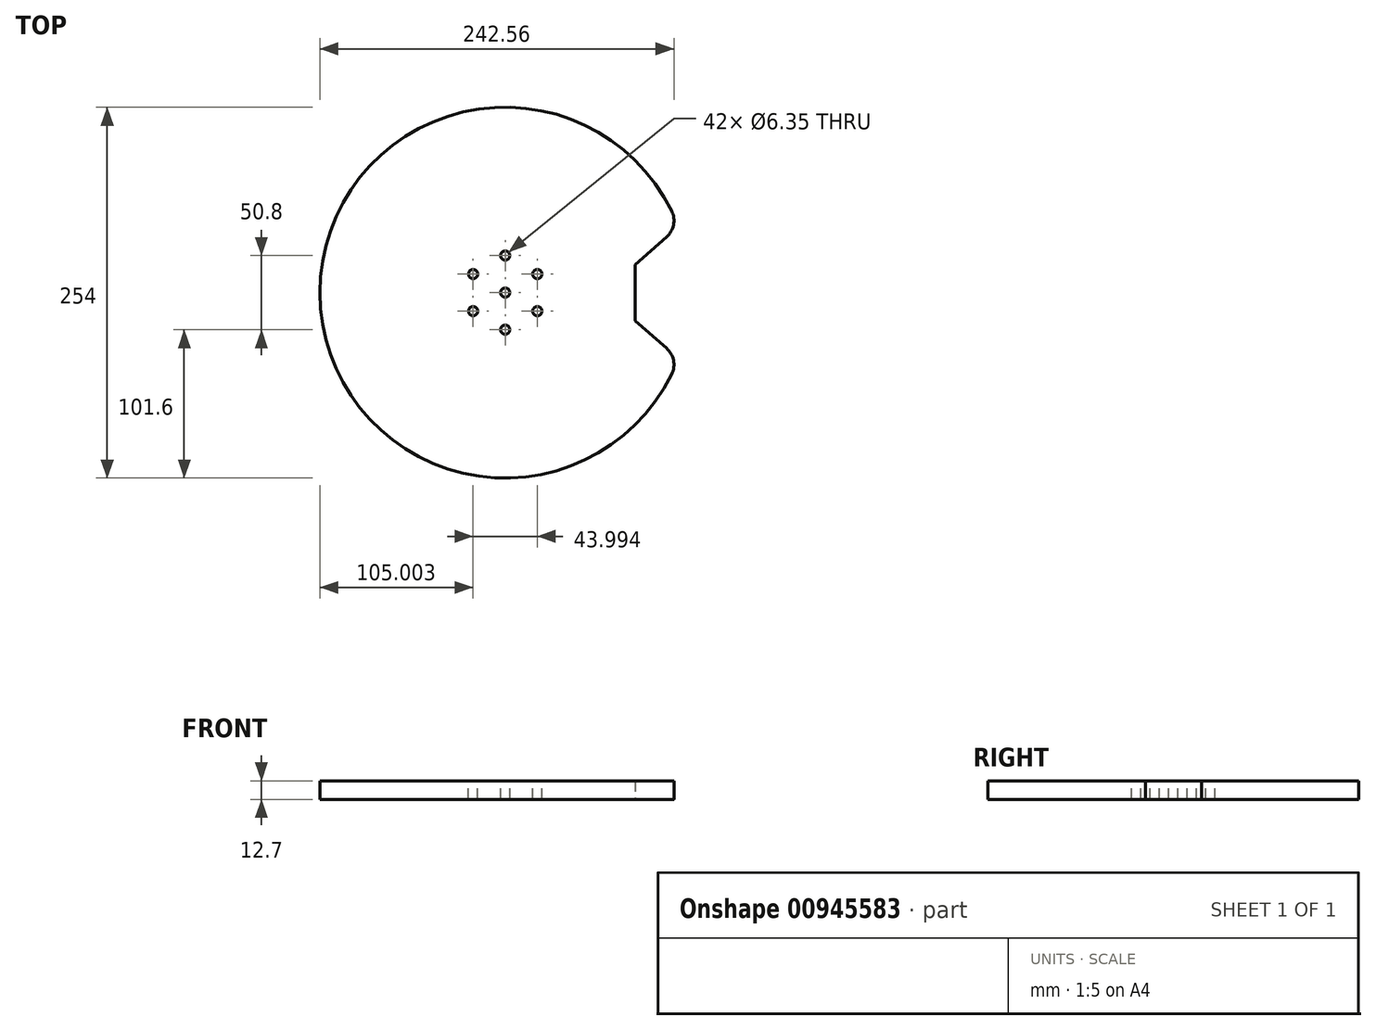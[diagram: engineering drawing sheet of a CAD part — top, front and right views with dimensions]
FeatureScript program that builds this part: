
annotation { "Feature Type Name" : "Feature", "Feature Type Description" : "" }
export const myFeature = defineFeature(function(context is Context, id is Id, definition is map)
    precondition{}
    {
        {
            var Q0;
            Q0=qCreatedBy(makeId("Top.planeOp"),FACE);
            var sketch = newSketch(context, id + "F0", { "sketchPlane" : qUnion([Q0])});
            skCircle(sketch, "E0", {"center": v(0, 0) * mm, "radius": 127 * mm});
            skLineSegment(sketch, "E1", {"start": v(88.9, 90.7) * mm, "end": v(88.9, -90.7) * mm});
            skLineSegment(sketch, "E2", {"start": v(88.9, 0) * mm, "end": v(127, 0) * mm});
            skSolve(sketch);
        }
        {
            var Q0;
            Q0=qCreatedBy(makeId("Top.planeOp"),FACE);
            var sketch = newSketch(context, id + "F1", { "sketchPlane" : qUnion([Q0])});
            skLineSegment(sketch, "E3", {"start": v(88.9, 19.18) * mm, "end": v(88.9, -19.18) * mm});
            skLineSegment(sketch, "E4", {"start": v(127, 52.5) * mm, "end": v(127, -52.5) * mm});
            skLineSegment(sketch, "E5", {"start": v(88.9, 19.18) * mm, "end": v(127, 52.5) * mm});
            skLineSegment(sketch, "E6", {"start": v(88.9, -19.18) * mm, "end": v(127, -52.5) * mm});
            skSolve(sketch);
        }
        {
            var Q0;
            {var subQ0=sQuery(id+"F0.wireOp",EDGE,"E1");var subQ1=sQuery(id+"F0.wireOp",EDGE,"E0");var subQ2=makeQuery(id+"F0.imprint","INTERSECT",VERTEX,{"disambiguationData":[OD(0.0)],"derivedFrom":[subQ1,subQ0]});Q0=makeQuery(id+"F0.imprint","IMPRINT",FACE,{"disambiguationData":[TD([[makeQuery(id+"F0.imprint","IMPRINT",EDGE,{"disambiguationData":[TD([[subQ2,-1.0]])],"derivedFrom":subQ1}),1.0]])]});}
            var Q1;
            {var subQ3=sQuery(id+"F0.wireOp",EDGE,"E2");Q1=makeQuery(id+"F0.imprint","IMPRINT",FACE,{"disambiguationData":[TD([[makeQuery(id+"F0.imprint","IMPRINT",EDGE,{"derivedFrom":subQ3}),1.0]])]});}
            var Q2;
            {var subQ3=sQuery(id+"F0.wireOp",EDGE,"E2");Q2=makeQuery(id+"F0.imprint","IMPRINT",FACE,{"disambiguationData":[TD([[makeQuery(id+"F0.imprint","IMPRINT",EDGE,{"derivedFrom":subQ3}),-1.0]])]});}
            extrude(context, id + "F2", {"entities" : qUnion([Q0, Q1, Q2]), "depth" : 12.7 * mm, "offsetDistance" : 25 * mm});
        }
        {
            var Q0;
            Q0=qSketchRegion(id+"F1",true);
            var Q1;
            Q1=makeQuery(id+"F2.opExtrude","CAP_FACE",FACE,{"disambiguationData":[OSD([sQuery(id+"F0.wireOp",EDGE,"E0")])],"isStart":false});
            extrude(context, id + "F3", {"entities" : qUnion([Q0]), "operationType" : NewBodyOperationType.REMOVE, "endBound" : BoundingType.UP_TO_SURFACE, "depth" : 25 * mm, "endBoundEntityFace" : qUnion([Q1]), "offsetDistance" : 25 * mm});
        }
        {
            var Q0;
            Q0=makeQuery(id+"F3.boolean.opBoolean","INTERSECT",EDGE,{"derivedFrom":[makeQuery(id+"F2.opExtrude","SWEPT_FACE",FACE,{"disambiguationData":[OSD([sQuery(id+"F0.wireOp",EDGE,"E0")])]}),makeQuery(id+"F3.opExtrude","SWEPT_FACE",FACE,{"disambiguationData":[OSD([sQuery(id+"F1.wireOp",EDGE,"E6")])]})]});
            var Q1;
            Q1=makeQuery(id+"F3.boolean.opBoolean","INTERSECT",EDGE,{"derivedFrom":[makeQuery(id+"F2.opExtrude","SWEPT_FACE",FACE,{"disambiguationData":[OSD([sQuery(id+"F0.wireOp",EDGE,"E0")])]}),makeQuery(id+"F3.opExtrude","SWEPT_FACE",FACE,{"disambiguationData":[OSD([sQuery(id+"F1.wireOp",EDGE,"E5")])]})]});
            fillet(context, id + "F4", {"entities" : qUnion([Q0, Q1]), "radius" : 15 * mm, "tangentPropagation" : true, "allowEdgeOverflow" : false});
        }
        {
            var Q0;
            Q0=makeQuery(id+"F2.opExtrude","CAP_FACE",FACE,{"disambiguationData":[OSD([sQuery(id+"F0.wireOp",EDGE,"E0")])],"isStart":false});
            var sketch = newSketch(context, id + "F5", { "sketchPlane" : qUnion([Q0])});
            skCircle(sketch, "E7", {"center": v(0, 0) * mm, "radius": 3.17 * mm});
            skCircle(sketch, "E8.cCircle", {"center": v(0, 0) * mm, "radius": 25.4 * mm, "construction": true});
            skLineSegment(sketch, "E8.0", {"start": v(0, -25.4) * mm, "end": v(-22, -12.7) * mm, "construction": true});
            skLineSegment(sketch, "E8.1", {"start": v(-22, -12.7) * mm, "end": v(-22, 12.7) * mm, "construction": true});
            skLineSegment(sketch, "E8.2", {"start": v(-22, 12.7) * mm, "end": v(0, 25.4) * mm, "construction": true});
            skLineSegment(sketch, "E8.3", {"start": v(0, 25.4) * mm, "end": v(22, 12.7) * mm, "construction": true});
            skLineSegment(sketch, "E8.4", {"start": v(22, 12.7) * mm, "end": v(22, -12.7) * mm, "construction": true});
            skLineSegment(sketch, "E8.5", {"start": v(22, -12.7) * mm, "end": v(0, -25.4) * mm, "construction": true});
            skCircle(sketch, "E9", {"center": v(0, 25.4) * mm, "radius": 3.18 * mm});
            skCircle(sketch, "E10.1.0", {"center": v(-22, 12.7) * mm, "radius": 3.18 * mm});
            skCircle(sketch, "E10.2.0", {"center": v(-22, -12.7) * mm, "radius": 3.18 * mm});
            skCircle(sketch, "E10.3.0", {"center": v(0, -25.4) * mm, "radius": 3.18 * mm});
            skCircle(sketch, "E10.4.0", {"center": v(22, -12.7) * mm, "radius": 3.18 * mm});
            skCircle(sketch, "E10.5.0", {"center": v(22, 12.7) * mm, "radius": 3.18 * mm});
            skSolve(sketch);
        }
        {
            var Q0;
            Q0=qSketchRegion(id+"F5",true);
            var Q1;
            Q1=makeQuery(id+"F2.opExtrude","CAP_FACE",FACE,{"disambiguationData":[OSD([sQuery(id+"F0.wireOp",EDGE,"E0")])],"isStart":true});
            extrude(context, id + "F6", {"entities" : qUnion([Q0]), "operationType" : NewBodyOperationType.REMOVE, "endBound" : BoundingType.UP_TO_SURFACE, "oppositeDirection" : true, "depth" : 25 * mm, "endBoundEntityFace" : qUnion([Q1]), "offsetDistance" : 25 * mm});
        }
    });
